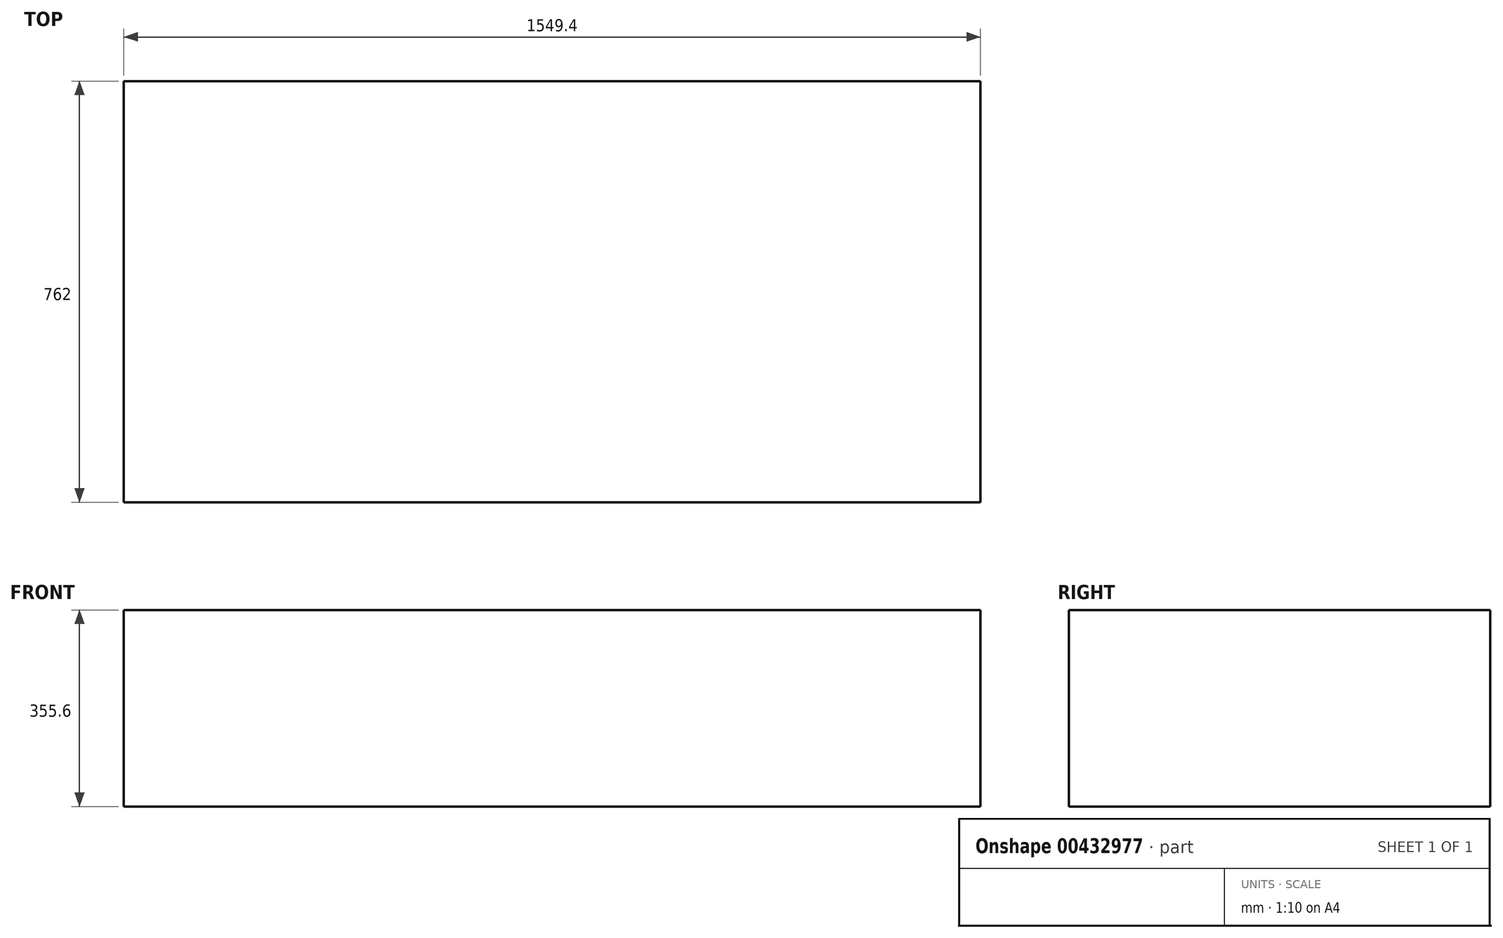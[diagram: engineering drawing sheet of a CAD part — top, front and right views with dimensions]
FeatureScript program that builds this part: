
annotation { "Feature Type Name" : "Feature", "Feature Type Description" : "" }
export const myFeature = defineFeature(function(context is Context, id is Id, definition is map)
    precondition{}
    {
        {
            var Q0;
            Q0=qCreatedBy(makeId("Top.planeOp"),FACE);
            var sketch = newSketch(context, id + "F0", { "sketchPlane" : qUnion([Q0])});
            skLineSegment(sketch, "E0.bottom", {"start": v(774.7, 381) * mm, "end": v(-774.7, 381) * mm});
            skLineSegment(sketch, "E0.top", {"start": v(774.7, -381) * mm, "end": v(-774.7, -381) * mm});
            skLineSegment(sketch, "E0.left", {"start": v(774.7, 381) * mm, "end": v(774.7, -381) * mm});
            skLineSegment(sketch, "E0.right", {"start": v(-774.7, 381) * mm, "end": v(-774.7, -381) * mm});
            skPoint(sketch, "E0.middle", {"position": v(0, 0) * mm});
            skSolve(sketch);
        }
        {
            var Q0;
            Q0=makeQuery(id+"F0.imprint","IMPRINT",FACE,{"disambiguationData":[TD([[makeQuery(id+"F0.imprint","IMPRINT",EDGE,{"derivedFrom":sQuery(id+"F0.wireOp",EDGE,"E0.bottom")}),1.0]])]});
            extrude(context, id + "F1", {"entities" : qUnion([Q0]), "depth" : 355.6 * mm});
        }
    });
